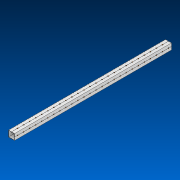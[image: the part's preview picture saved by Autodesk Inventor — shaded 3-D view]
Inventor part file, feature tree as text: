
AUTODESK INVENTOR PART (.ipt)
format: ipt  version: 2022.2 (Build 262287000, 287)  size: 855,040 bytes
history: native  units: in
note: dims shown in document units (in); Inventor stores cm internally (conversion verified against a paired STEP export)
features: other x52, pattern_linear x2, extrude x1, sketch x1
ambient origin geometry x8: Origin, YZ Plane, XZ Plane, XY Plane, X Axis, Y Axis, Z Axis, Center Point
bodies: Solid1 (feature_tree)
feature tree (56):
  extrude  "Extrusion1"  TaperAngle=0.0deg  [1 undecoded]
  other  "Work Axis1"
  other  "Work Axis2"
  pattern_linear  "Rectangular Pattern1"  Count1=26  [1 undecoded]
  pattern_linear  "Rectangular Pattern2"  Spacing1=1.0in  [1 undecoded]
  sketch  "Sketch1"  dims[d0=33.0in d1=0.0in d2=10.2362in d4=1.0in d5=9.8425in d7=1.0in]
  other  "Work Axis3"
  other  "Work Axis4"
  other  "Work Axis5"
  other  "Work Axis6"
  other  "Work Axis7"
  other  "Work Axis8"
  other  "Work Axis9"
  other  "Work Axis10"
  other  "Work Axis11"
  other  "Work Axis12"
  other  "Work Axis13"
  other  "Work Axis14"
  other  "Work Axis15"
  other  "Work Axis16"
  other  "Work Axis17"
  other  "Work Axis18"
  other  "Work Axis19"
  other  "Work Axis20"
  other  "Work Axis21"
  other  "Work Axis22"
  other  "Work Axis23"
  other  "Work Axis24"
  other  "Work Axis25"
  other  "Work Axis26"
  other  "Work Axis27"
  other  "Work Axis28"
  other  "Work Axis29"
  other  "Work Axis63"
  other  "Work Axis64"
  other  "Work Axis65"
  other  "Work Axis66"
  other  "Work Axis67"
  other  "Work Axis68"
  other  "Work Axis69"
  other  "Work Axis70"
  other  "Work Axis71"
  other  "Work Axis72"
  other  "Work Axis73"
  other  "Work Axis74"
  other  "Work Axis75"
  other  "Work Axis76"
  other  "Work Axis77"
  other  "Work Axis78"
  other  "Work Axis79"
  other  "Work Axis80"
  other  "Work Axis81"
  other  "Work Axis82"
  other  "Work Axis83"
  other  "Work Axis84"
  other  "LPattern2"
note: 3 required parameter values undecoded (feature->parameter linkage not recoverable at this tier; creation-order binding heuristic only, values carry confidence <= 0.55)
